# Revit family: Sanitary_Bidets_Sanindusa_Look-Wall-Mounted-Bidet-With-Holes-For-Lid
name_source: partatom
category: Plumbing Fixtures
revit_build: Autodesk Revit 2018 (Build: 20170223_1515(x64)
units: mm (PartAtom-declared; Revit-internal decimal feet)

## family parameters
Always vertical = Yes
Cut with Voids When Loaded = No
Host = Wall
OmniClass Number = 23.45.00.00
OmniClass Title = Sanitary, Laundry, and Cleaning Equipment
Part Type = Normal
Room Calculation Point = No
Round Connector Dimension = Use Diameter
Shared = No

## types (1)
- SaninusaBidé134455004
    AssetType = Fixed
    BIMObjectName = Bidet_Look
    BidetMounting = wallhung
    Category = Pr_40_20_06_11,Bidets
    CodePerformance = EN 14528:2007 - CL 25
    Color = White
    Constituents = Compatible bidet lid (not included): 2344100-Look bidet lid with clipoff and slowclose system. Compatible suport frames (not inluded): 439-Metal support for wall mounted bidet for pladur, 430-Metal support for wall mounted bidet. 48011-chromed embellishment ring (included)
    Cost = 0 $
    Description = Suspended Bidet Look with holes for lid
    DrainSize = 44 mm  [stored 0.144357 ft]
    Edition number = 1
    Element Type = BIDET: Waste water appliance for washing the excretory organs while sitting astride the bowl (BS6100)
    Features = Wall mounted bidet, easy to clean. It's the perfect solution. And its modern style fits beautifully with contemporary bathrooms.
    Finish = Gloss
    InletDiameter = 35 mm
    Installation Instructions = https://www.tec.sanindusa.pt
    InstallationDate = 1900-12-31T23:59:59
    Manufacturer = Sanindusa
    ManufacturerName = Sanindusa
    ManufacturerURL = www.tec.sanindusa.pt
    Material = Vitreous China
    ModelNumber = 134455004
    ModelReference = Look
    Name = Bidet_Look
    NominalHeight = 300 mm
    NominalLength = 342 mm
    NominalWidth = 503 mm
    Pre-defined type (IFC) = BIDET
    Product Guid = 471586fb-df95-40a7-ae97-a31b776a3e45
    Product data url = https://bimobject.com
    ProductInformation = http://www.tec.sanindusa.pt
    ProductionYear = 2017
    Size = 342x503x300
    SpilloverLevel = 116
    SustainabilityPerformance = n/a
n/a
    Type (IFC) = IfcSanitaryTerminalType
    URL = www.tec.sanindusa.pt
    Uniclass2015Code = Pr_40_20_06_11
    Uniclass2015Title = Bidets
    Uniclass2015Version = Products v1.6
    Version = 2
    WarrantyDescription = https://www.tec.sanindusa.pt
The warranty will come into force from the moment the warranty detachable bulletin that accompanies the product is received at Sanindusa or from the moment the product is sold to the distributer.
Only if the customer issues a writen and justified (Country laws, state laws, commercial strategy) request to Sanindusa, may the above mentioned warranties be the object of a possible change. 2 Year warranty for electronic components.
    WarrantyDurationParts = 5
    WarrantyDurationUnit = year
    WarrantyStartDate = 1900-12-31T23:59:59
    Weight = 20.00 kg

note: [stored X ft] marks values corroborated as IEEE doubles in the binary element streams (Revit-internal decimal feet)

## geometry (parser evidence)
native form markers: Sweep x7
no freeform markers — native parametric forms only
